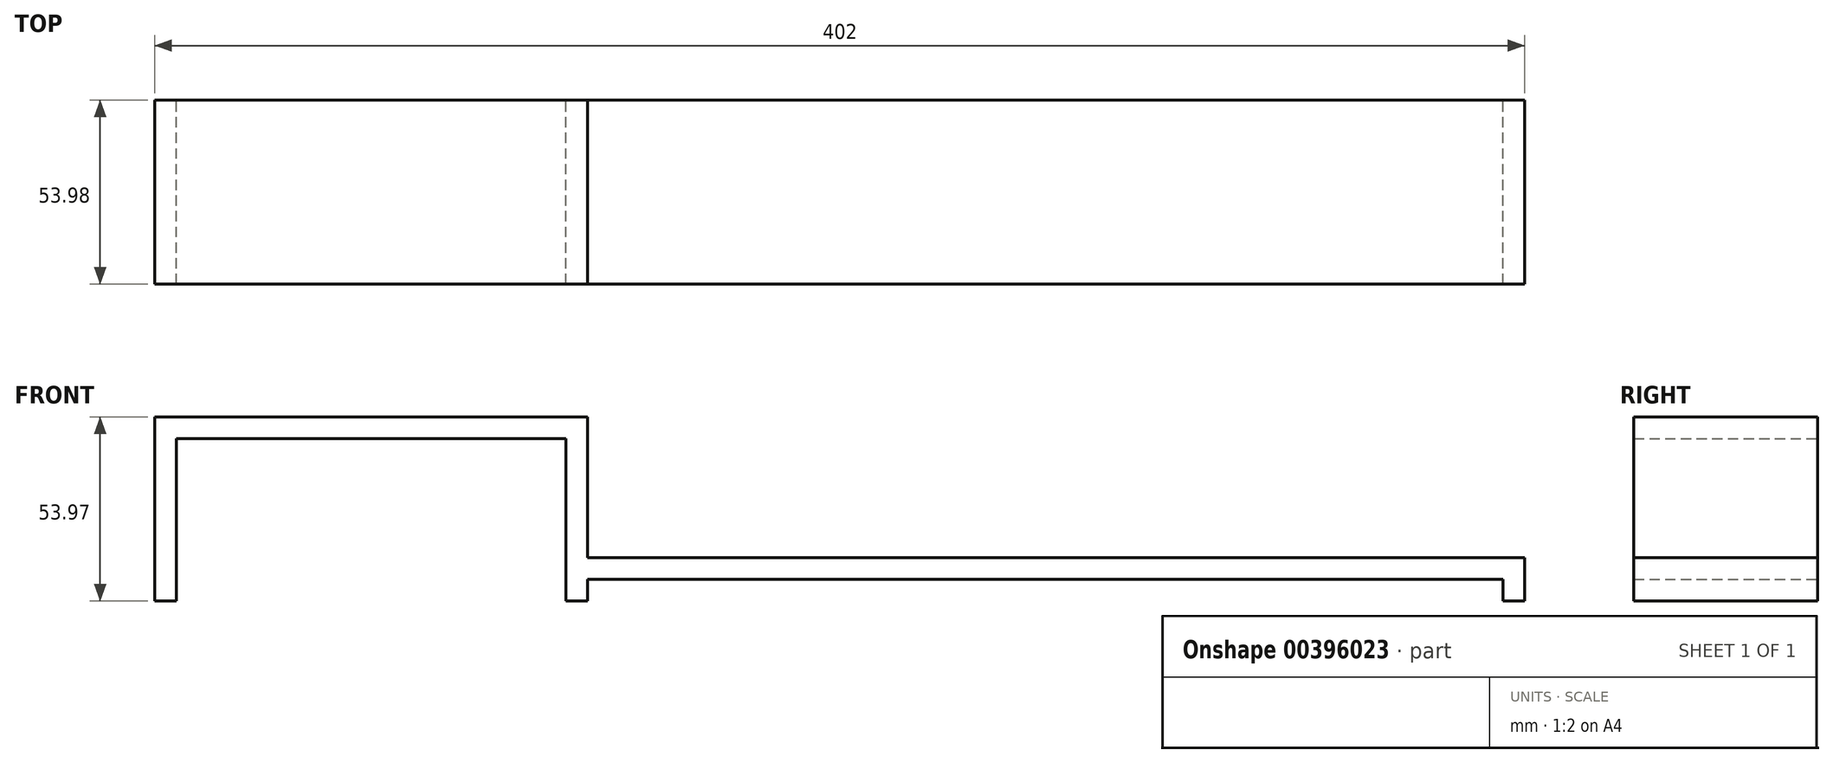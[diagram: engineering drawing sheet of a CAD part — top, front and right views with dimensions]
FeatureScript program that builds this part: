
annotation { "Feature Type Name" : "Feature", "Feature Type Description" : "" }
export const myFeature = defineFeature(function(context is Context, id is Id, definition is map)
    precondition{}
    {
        {
            var Q0;
            Q0=qCreatedBy(makeId("Front.planeOp"),FACE);
            var sketch = newSketch(context, id + "F0", { "sketchPlane" : qUnion([Q0])});
            skLineSegment(sketch, "E0.bottom", {"start": v(6.35, 0) * mm, "end": v(275, 0) * mm});
            skLineSegment(sketch, "E0.top", {"start": v(6.35, 6.35) * mm, "end": v(281.35, 6.35) * mm});
            skLineSegment(sketch, "E0.left", {"start": v(0, 0) * mm, "end": v(0, 6.35) * mm});
            skLineSegment(sketch, "E0.right", {"start": v(281.35, 0) * mm, "end": v(281.35, 6.35) * mm});
            skLineSegment(sketch, "E1.bottom", {"start": v(-120.65, 47.63) * mm, "end": v(6.35, 47.63) * mm});
            skLineSegment(sketch, "E1.top", {"start": v(-114.3, 41.28) * mm, "end": v(0, 41.28) * mm});
            skLineSegment(sketch, "E1.left", {"start": v(-120.65, 47.63) * mm, "end": v(-120.65, 41.28) * mm});
            skLineSegment(sketch, "E1.right", {"start": v(6.35, 47.63) * mm, "end": v(6.35, 41.28) * mm});
            skLineSegment(sketch, "E2.left", {"start": v(6.35, 41.28) * mm, "end": v(6.35, 6.35) * mm});
            skLineSegment(sketch, "E2.right", {"start": v(0, 41.28) * mm, "end": v(0, 6.35) * mm});
            skLineSegment(sketch, "E3.bottom", {"start": v(-120.65, 47.63) * mm, "end": v(-114.3, 47.63) * mm});
            skLineSegment(sketch, "E3.top", {"start": v(-120.65, -6.35) * mm, "end": v(-114.3, -6.35) * mm});
            skLineSegment(sketch, "E3.left", {"start": v(-120.65, 47.63) * mm, "end": v(-120.65, -6.35) * mm});
            skLineSegment(sketch, "E3.right", {"start": v(-114.3, 41.28) * mm, "end": v(-114.3, -6.35) * mm});
            skLineSegment(sketch, "E4.top", {"start": v(281.35, -6.35) * mm, "end": v(275, -6.35) * mm});
            skLineSegment(sketch, "E4.left", {"start": v(281.35, 0) * mm, "end": v(281.35, -6.35) * mm});
            skLineSegment(sketch, "E4.right", {"start": v(275, 0) * mm, "end": v(275, -6.35) * mm});
            skLineSegment(sketch, "E5.top", {"start": v(0, -6.35) * mm, "end": v(6.35, -6.35) * mm});
            skLineSegment(sketch, "E5.left", {"start": v(0, 0) * mm, "end": v(0, -6.35) * mm});
            skLineSegment(sketch, "E5.right", {"start": v(6.35, 0) * mm, "end": v(6.35, -6.35) * mm});
            skSolve(sketch);
        }
        {
            var Q0;
            Q0 = qSketchRegion(id + "F0", true);
            extrude(context, id + "F1", {"entities" : qUnion([Q0]), "depth" : 53.97 * mm, "offsetDistance" : 25.4 * mm});
        }
    });
